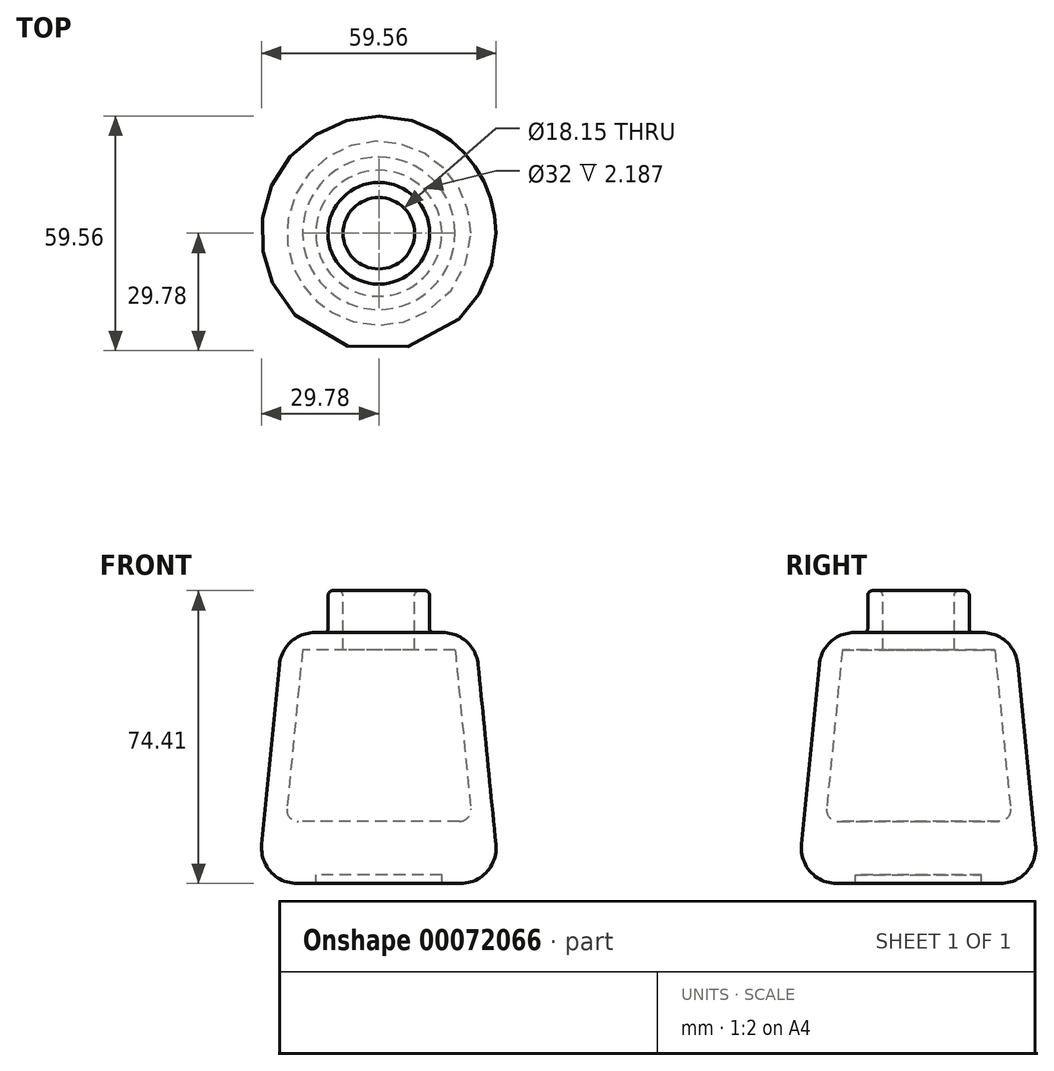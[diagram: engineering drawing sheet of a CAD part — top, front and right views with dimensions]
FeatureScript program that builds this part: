
annotation { "Feature Type Name" : "Feature", "Feature Type Description" : "" }
export const myFeature = defineFeature(function(context is Context, id is Id, definition is map)
    precondition{}
    {
        {
            var Q0;
            Q0=qCreatedBy(makeId("Front.planeOp"),FACE);
            var sketch = newSketch(context, id + "F0", { "sketchPlane" : qUnion([Q0])});
            skLineSegment(sketch, "E0", {"start": v(0, 4) * mm, "end": v(16, 4) * mm});
            skPoint(sketch, "E1.visualSharp", {"position": v(20, 4) * mm});
            skLineSegment(sketch, "E2", {"start": v(30.71, 1.81) * mm, "end": v(24.44, 65.55) * mm});
            skLineSegment(sketch, "E3", {"start": v(24.44, 65.55) * mm, "end": v(12.9, 65.55) * mm});
            skLineSegment(sketch, "E4", {"start": v(12.9, 65.55) * mm, "end": v(12.9, 76.22) * mm});
            skLineSegment(sketch, "E5", {"start": v(12.9, 76.22) * mm, "end": v(9.07, 76.22) * mm});
            skLineSegment(sketch, "E6", {"start": v(9.07, 76.22) * mm, "end": v(9.07, 61.09) * mm});
            skLineSegment(sketch, "E7", {"start": v(9.07, 61.09) * mm, "end": v(19.39, 61.09) * mm});
            skLineSegment(sketch, "E8", {"start": v(19.39, 61.09) * mm, "end": v(23.35, 20.78) * mm});
            skLineSegment(sketch, "E9", {"start": v(20.45, 17.57) * mm, "end": v(0, 17.57) * mm});
            skPoint(sketch, "E10.visualSharp", {"position": v(23.67, 17.57) * mm});
            skArc(sketch, "E10.filletArc", {"start": v(20.45, 17.57) * mm, "mid": v(22.61, 18.53) * mm, "end": v(23.35, 20.78) * mm});
            skLineSegment(sketch, "E11", {"start": v(0, 4) * mm, "end": v(0, 17.57) * mm});
            skLineSegment(sketch, "E12", {"start": v(0, 61.42) * mm, "end": v(0, 27.56) * mm, "construction": true});
            skLineSegment(sketch, "E13", {"start": v(16, 4) * mm, "end": v(16, 1.81) * mm});
            skLineSegment(sketch, "E14", {"start": v(16, 1.81) * mm, "end": v(30.71, 1.81) * mm});
            skSolve(sketch);
        }
        {
            var Q0;
            Q0=makeQuery(id+"F0.imprint","IMPRINT",FACE,{"disambiguationData":[TD([[makeQuery(id+"F0.imprint","IMPRINT",EDGE,{"derivedFrom":sQuery(id+"F0.wireOp",EDGE,"E0")}),1.0]])]});
            var Q1;
            Q1=sQuery(id+"F0.wireOp",EDGE,"E12");
            revolve(context, id + "F1", {"entities" : qUnion([Q0]), "axis" : qUnion([Q1]), "revolveType" : RevolveType.FULL});
        }
        {
            var Q0;
            Q0=makeQuery(id+"F1.opRevolve","SWEPT_EDGE",EDGE,{"disambiguationData":[OSD([sQuery(id+"F0.wireOp",EDGE,"E2"),sQuery(id+"F0.wireOp",EDGE,"E14")])]});
            var Q1;
            Q1=makeQuery(id+"F1.opRevolve","SWEPT_EDGE",EDGE,{"disambiguationData":[OSD([sQuery(id+"F0.wireOp",EDGE,"E2"),sQuery(id+"F0.wireOp",EDGE,"E3")])]});
            fillet(context, id + "F2", {"entities" : qUnion([Q0, Q1]), "radius" : 9 * mm, "tangentPropagation" : true, "allowEdgeOverflow" : false});
        }
        {
            var Q0;
            Q0=makeQuery(id+"F1.opRevolve","SWEPT_EDGE",EDGE,{"disambiguationData":[OSD([sQuery(id+"F0.wireOp",EDGE,"E4"),sQuery(id+"F0.wireOp",EDGE,"E5")])]});
            var Q1;
            Q1=makeQuery(id+"F1.opRevolve","SWEPT_EDGE",EDGE,{"disambiguationData":[OSD([sQuery(id+"F0.wireOp",EDGE,"E5"),sQuery(id+"F0.wireOp",EDGE,"E6")])]});
            fillet(context, id + "F3", {"entities" : qUnion([Q0, Q1]), "radius" : 1.3 * mm, "tangentPropagation" : true, "allowEdgeOverflow" : false});
        }
        {
            var Q0;
            Q0=makeQuery(id+"F1.opRevolve","SWEPT_EDGE",EDGE,{"disambiguationData":[OSD([sQuery(id+"F0.wireOp",EDGE,"E3"),sQuery(id+"F0.wireOp",EDGE,"E4")])]});
            fillet(context, id + "F4", {"entities" : qUnion([Q0]), "radius" : 1 * mm, "tangentPropagation" : true, "allowEdgeOverflow" : false});
        }
    });
